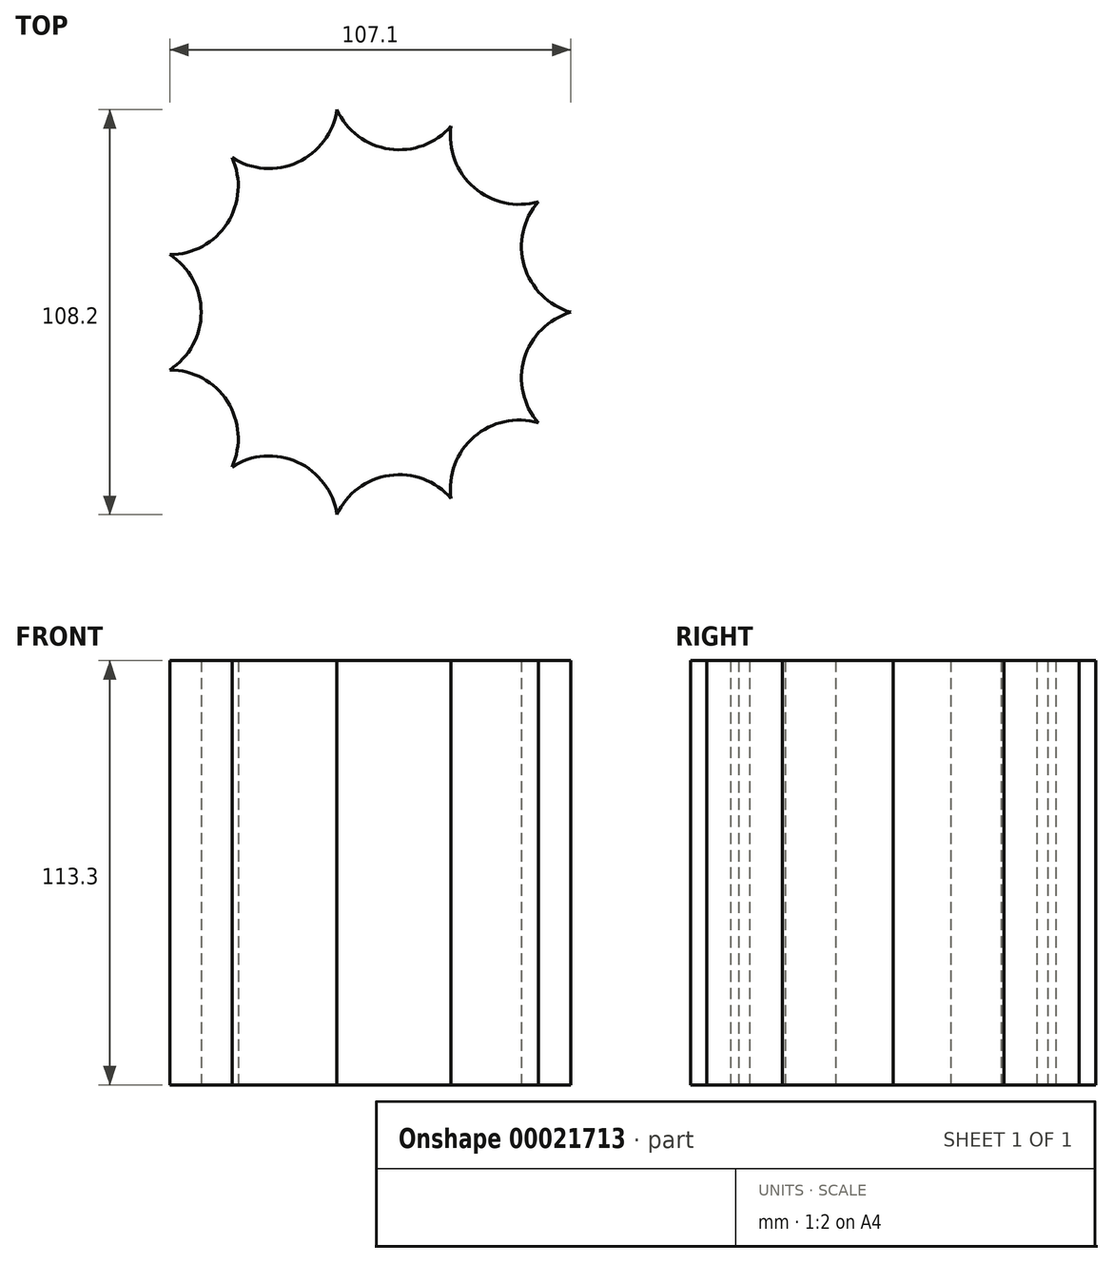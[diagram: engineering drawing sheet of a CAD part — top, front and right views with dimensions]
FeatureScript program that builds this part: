
annotation { "Feature Type Name" : "Feature", "Feature Type Description" : "" }
export const myFeature = defineFeature(function(context is Context, id is Id, definition is map)
    precondition{}
    {
        {
            var Q0;
            Q0=qCreatedBy(makeId("Top.planeOp"),FACE);
            var sketch = newSketch(context, id + "F0", { "sketchPlane" : qUnion([Q0])});
            skCircle(sketch, "E0.cCircle", {"center": v(0, 0) * mm, "radius": 62.34 * mm, "construction": true});
            skLineSegment(sketch, "E0.0", {"start": v(-62.34, -18.3) * mm, "end": v(-62.34, 18.3) * mm});
            skLineSegment(sketch, "E0.1", {"start": v(-62.34, 18.3) * mm, "end": v(-42.55, 49.1) * mm});
            skLineSegment(sketch, "E0.2", {"start": v(-42.55, 49.1) * mm, "end": v(-9.25, 64.3) * mm});
            skLineSegment(sketch, "E0.3", {"start": v(-9.25, 64.3) * mm, "end": v(26.99, 59.1) * mm});
            skLineSegment(sketch, "E0.4", {"start": v(26.99, 59.1) * mm, "end": v(54.66, 35.13) * mm});
            skLineSegment(sketch, "E0.5", {"start": v(54.66, 35.13) * mm, "end": v(64.97, 0) * mm});
            skLineSegment(sketch, "E0.6", {"start": v(64.97, 0) * mm, "end": v(54.66, -35.13) * mm});
            skLineSegment(sketch, "E0.7", {"start": v(54.66, -35.13) * mm, "end": v(26.99, -59.1) * mm});
            skLineSegment(sketch, "E0.8", {"start": v(26.99, -59.1) * mm, "end": v(-9.25, -64.3) * mm});
            skLineSegment(sketch, "E0.9", {"start": v(-9.25, -64.3) * mm, "end": v(-42.55, -49.1) * mm});
            skLineSegment(sketch, "E0.10", {"start": v(-42.55, -49.1) * mm, "end": v(-62.34, -18.3) * mm});
            skPoint(sketch, "E0.0.midPoint", {"position": v(-62.34, 0) * mm});
            skCircle(sketch, "E1", {"center": v(-62.34, 0) * mm, "radius": 18.3 * mm});
            skCircle(sketch, "E2", {"center": v(-52.44, -33.7) * mm, "radius": 18.3 * mm});
            skCircle(sketch, "E3", {"center": v(-52.44, 33.7) * mm, "radius": 18.3 * mm});
            skCircle(sketch, "E4", {"center": v(-25.9, 56.7) * mm, "radius": 18.3 * mm});
            skCircle(sketch, "E5", {"center": v(8.87, 61.7) * mm, "radius": 18.3 * mm});
            skCircle(sketch, "E6", {"center": v(40.82, 47.11) * mm, "radius": 18.3 * mm});
            skCircle(sketch, "E7", {"center": v(59.81, 17.56) * mm, "radius": 18.3 * mm});
            skCircle(sketch, "E8", {"center": v(59.81, -17.56) * mm, "radius": 18.3 * mm});
            skCircle(sketch, "E9", {"center": v(40.82, -47.11) * mm, "radius": 18.3 * mm});
            skCircle(sketch, "E10", {"center": v(8.87, -61.7) * mm, "radius": 18.3 * mm});
            skCircle(sketch, "E11", {"center": v(-25.9, -56.7) * mm, "radius": 18.3 * mm});
            skSolve(sketch);
        }
        {
            var Q0;
            {var subQ17=sQuery(id+"F0.wireOp",EDGE,"E3");var subQ19=sQuery(id+"F0.wireOp",EDGE,"E1");var subQ20=makeQuery(id+"F0.imprint","INTERSECT",VERTEX,{"derivedFrom":[subQ19,subQ17]});Q0=makeQuery(id+"F0.imprint","IMPRINT",FACE,{"disambiguationData":[TD([[makeQuery(id+"F0.imprint","IMPRINT",EDGE,{"disambiguationData":[TD([[subQ20,1.0]])],"derivedFrom":subQ19}),-1.0]])]});}
            extrude(context, id + "F1", {"entities" : qUnion([Q0]), "depth" : 113.3 * mm});
        }
    });
